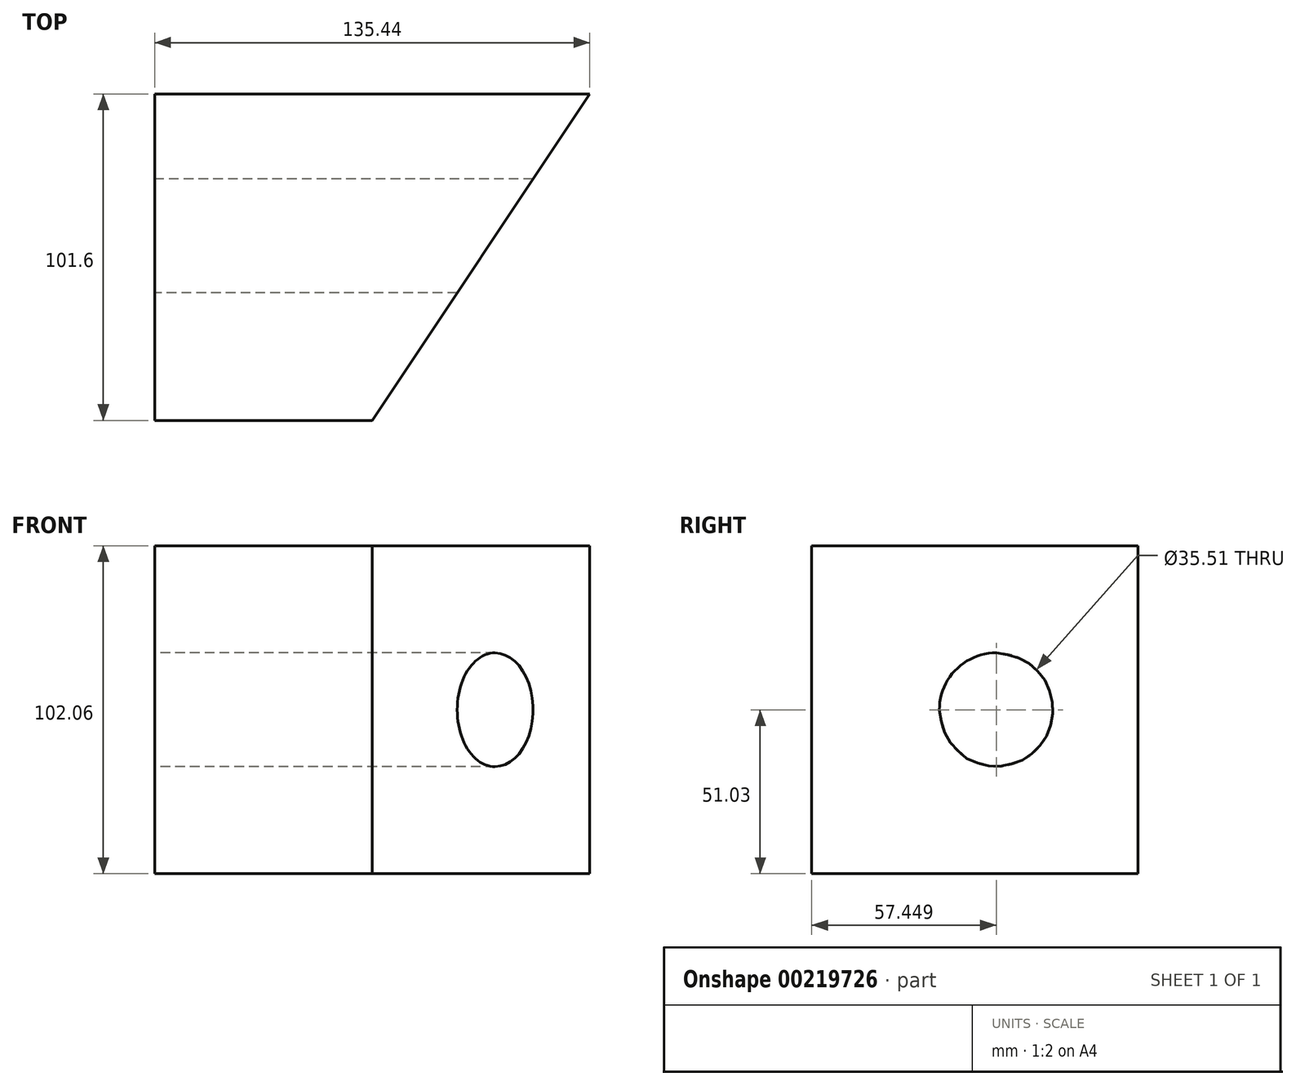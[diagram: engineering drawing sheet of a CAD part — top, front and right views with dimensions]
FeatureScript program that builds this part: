
annotation { "Feature Type Name" : "Feature", "Feature Type Description" : "" }
export const myFeature = defineFeature(function(context is Context, id is Id, definition is map)
    precondition{}
    {
        {
            var Q0;
            Q0=qCreatedBy(makeId("Front.planeOp"),FACE);
            var sketch = newSketch(context, id + "F0", { "sketchPlane" : qUnion([Q0])});
            skLineSegment(sketch, "E0.bottom", {"start": v(67.72, -51.03) * mm, "end": v(-67.72, -51.03) * mm});
            skLineSegment(sketch, "E0.top", {"start": v(67.72, 51.03) * mm, "end": v(-67.72, 51.03) * mm});
            skLineSegment(sketch, "E0.left", {"start": v(67.72, -51.03) * mm, "end": v(67.72, 51.03) * mm});
            skLineSegment(sketch, "E0.right", {"start": v(-67.72, -51.03) * mm, "end": v(-67.72, 51.03) * mm});
            skPoint(sketch, "E0.middle", {"position": v(0, 0) * mm});
            skSolve(sketch);
        }
        {
            var Q0;
            Q0=makeQuery(id+"F0.imprint","IMPRINT",FACE,{"disambiguationData":[TD([[makeQuery(id+"F0.imprint","IMPRINT",EDGE,{"derivedFrom":sQuery(id+"F0.wireOp",EDGE,"E0.bottom")}),-1.0]])]});
            extrude(context, id + "F1", {"entities" : qUnion([Q0]), "depth" : 101.6 * mm});
        }
        {
            var Q0;
            Q0=makeQuery(id+"F1.opExtrude","SWEPT_FACE",FACE,{"disambiguationData":[OSD([sQuery(id+"F0.wireOp",EDGE,"E0.bottom")])]});
            var sketch = newSketch(context, id + "F2", { "sketchPlane" : qUnion([Q0])});
            skLineSegment(sketch, "E1.0", {"start": v(67.72, 101.6) * mm, "end": v(-67.72, 101.6) * mm});
            skLineSegment(sketch, "E2.0", {"start": v(67.72, 101.6) * mm, "end": v(67.72, 0) * mm});
            skLineSegment(sketch, "E3", {"start": v(67.72, 0) * mm, "end": v(0, 101.6) * mm});
            skSolve(sketch);
        }
        {
            var Q0;
            Q0 = qSketchRegion(id + "F2", true);
            extrude(context, id + "F3", {"entities" : qUnion([Q0]), "operationType" : NewBodyOperationType.REMOVE, "endBound" : BoundingType.THROUGH_ALL, "oppositeDirection" : true, "depth" : 25.4 * mm});
        }
        {
            var Q0;
            Q0=makeQuery(id+"F1.opExtrude","SWEPT_FACE",FACE,{"disambiguationData":[OSD([sQuery(id+"F0.wireOp",EDGE,"E0.right")])]});
            var sketch = newSketch(context, id + "F4", { "sketchPlane" : qUnion([Q0])});
            skCircle(sketch, "E4", {"center": v(44.15, 0) * mm, "radius": 17.75 * mm});
            skSolve(sketch);
        }
        {
            var Q0;
            Q0=makeQuery(id+"F4.imprint","IMPRINT",FACE,{"disambiguationData":[TD([[makeQuery(id+"F4.imprint","IMPRINT",EDGE,{"derivedFrom":sQuery(id+"F4.wireOp",EDGE,"E4")}),1.0]])]});
            extrude(context, id + "F5", {"entities" : qUnion([Q0]), "operationType" : NewBodyOperationType.REMOVE, "endBound" : BoundingType.THROUGH_ALL, "oppositeDirection" : true, "depth" : 25.4 * mm});
        }
    });
